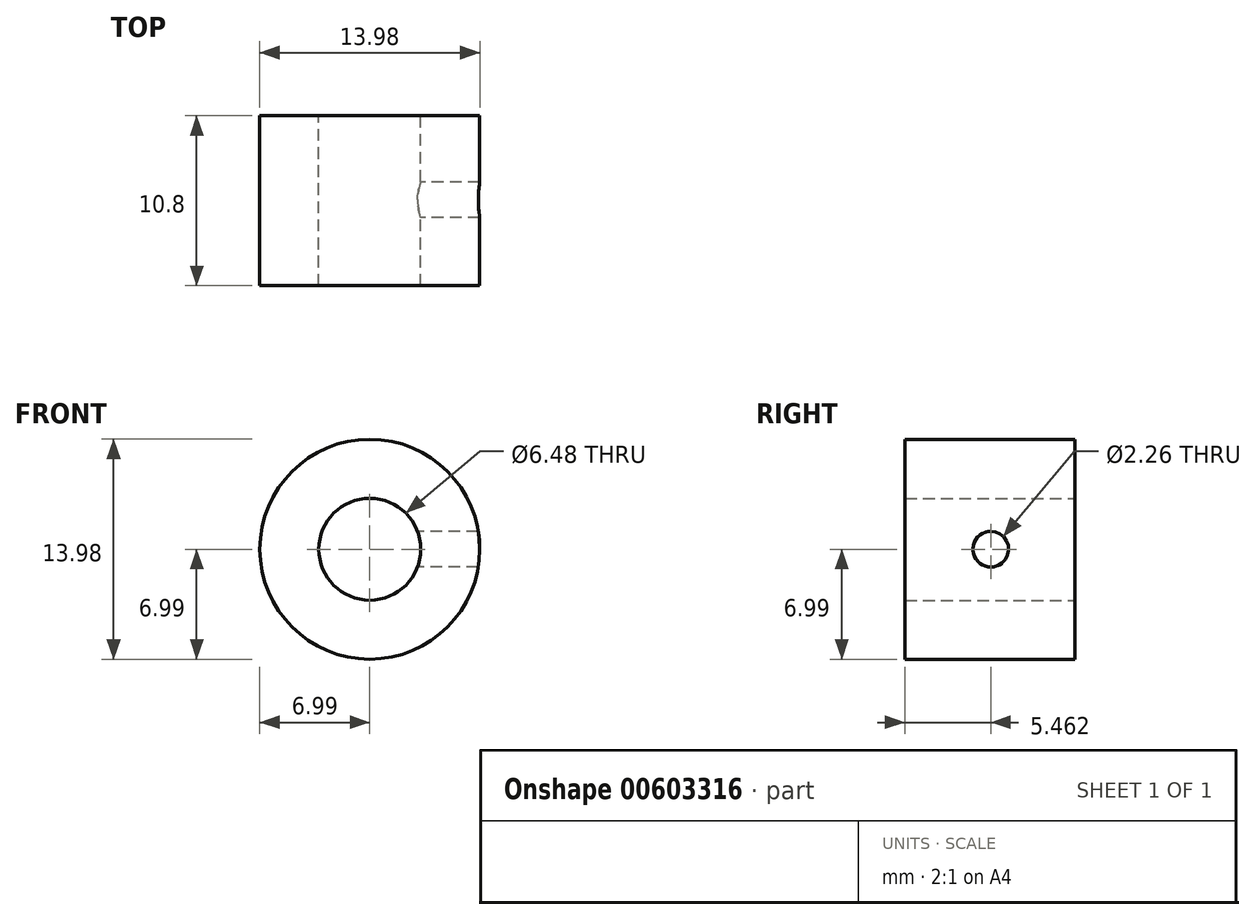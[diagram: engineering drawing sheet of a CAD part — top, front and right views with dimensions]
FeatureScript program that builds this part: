
annotation { "Feature Type Name" : "Feature", "Feature Type Description" : "" }
export const myFeature = defineFeature(function(context is Context, id is Id, definition is map)
    precondition{}
    {
        {
            var Q0;
            Q0=qCreatedBy(makeId("Front.planeOp"),FACE);
            var sketch = newSketch(context, id + "F0", { "sketchPlane" : qUnion([Q0])});
            skCircle(sketch, "E0", {"center": v(0, 0) * mm, "radius": 6.99 * mm});
            skCircle(sketch, "E1", {"center": v(0, 0) * mm, "radius": 3.24 * mm});
            skSolve(sketch);
        }
        {
            var Q0;
            Q0 = qSketchRegion(id + "F0", true);
            extrude(context, id + "F1", {"entities" : qUnion([Q0]), "depth" : 10.8 * mm, "offsetDistance" : 25 * mm});
        }
        {
            var Q0;
            Q0=qCreatedBy(makeId("Right.planeOp"),FACE);
            var sketch = newSketch(context, id + "F2", { "sketchPlane" : qUnion([Q0])});
            skCircle(sketch, "E2", {"center": v(-5.34, 0) * mm, "radius": 1.22 * mm});
            skSolve(sketch);
        }
        {
            var Q0;
            Q0=sQuery(id+"F2.wireOp",VERTEX,"E2.center");
            var Q1;
            Q1=makeQuery(id+"F1.opExtrude","SWEPT_BODY",BODY,{"disambiguationData":[OSD([sQuery(id+"F0.wireOp",EDGE,"E0"),sQuery(id+"F0.wireOp",EDGE,"E1")])]});
            hole(context, id + "F3", {"style" : HoleStyle.SIMPLE, "endStyle" : HoleEndStyle.BLIND, "oppositeDirection" : true, "standardTappedOrClearance" : lookupTablePath({ "standard" : "ANSI", "engagement" : "75%", "pitch" : "40 tpi", "size" : "#4", "type" : "Tapped" }), "standardBlindInLast" : lookupTablePath({ "standard" : "ANSI", "engagement" : "75%", "pitch" : "40 tpi", "size" : "#4", "type" : "Tapped" }), "holeDiameter" : 2.26 * mm, "majorDiameter" : 2.84 * mm, "showTappedDepth" : true, "holeDepth" : 13.9 * mm, "isTappedThrough" : true, "tappedDepth" : 12 * mm, "tapClearance" : 3, "locations" : qUnion([Q0]), "scope" : qUnion([Q1])});
        }
    });
